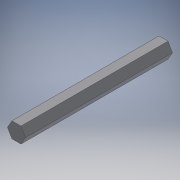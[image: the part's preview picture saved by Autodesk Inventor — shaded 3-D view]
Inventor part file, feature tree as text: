
AUTODESK INVENTOR PART (.ipt)
format: ipt  version: 2018 (Build 220112000, 112)  size: 94,208 bytes
history: native  units: in
note: dims shown in document units (in); Inventor stores cm internally (conversion verified against a paired STEP export)
features: extrude x1, sketch x1
ambient origin geometry x8: Origin, YZ Plane, XZ Plane, XY Plane, X Axis, Y Axis, Z Axis, Center Point
bodies: Solid1 (feature_tree)
feature tree (2):
  extrude  "Extrusion1"  Depth=4.697in TaperAngle=0.0deg
  sketch  "Sketch1"  dims[d0=0.5in d1=4.697in d2=0.0in]
